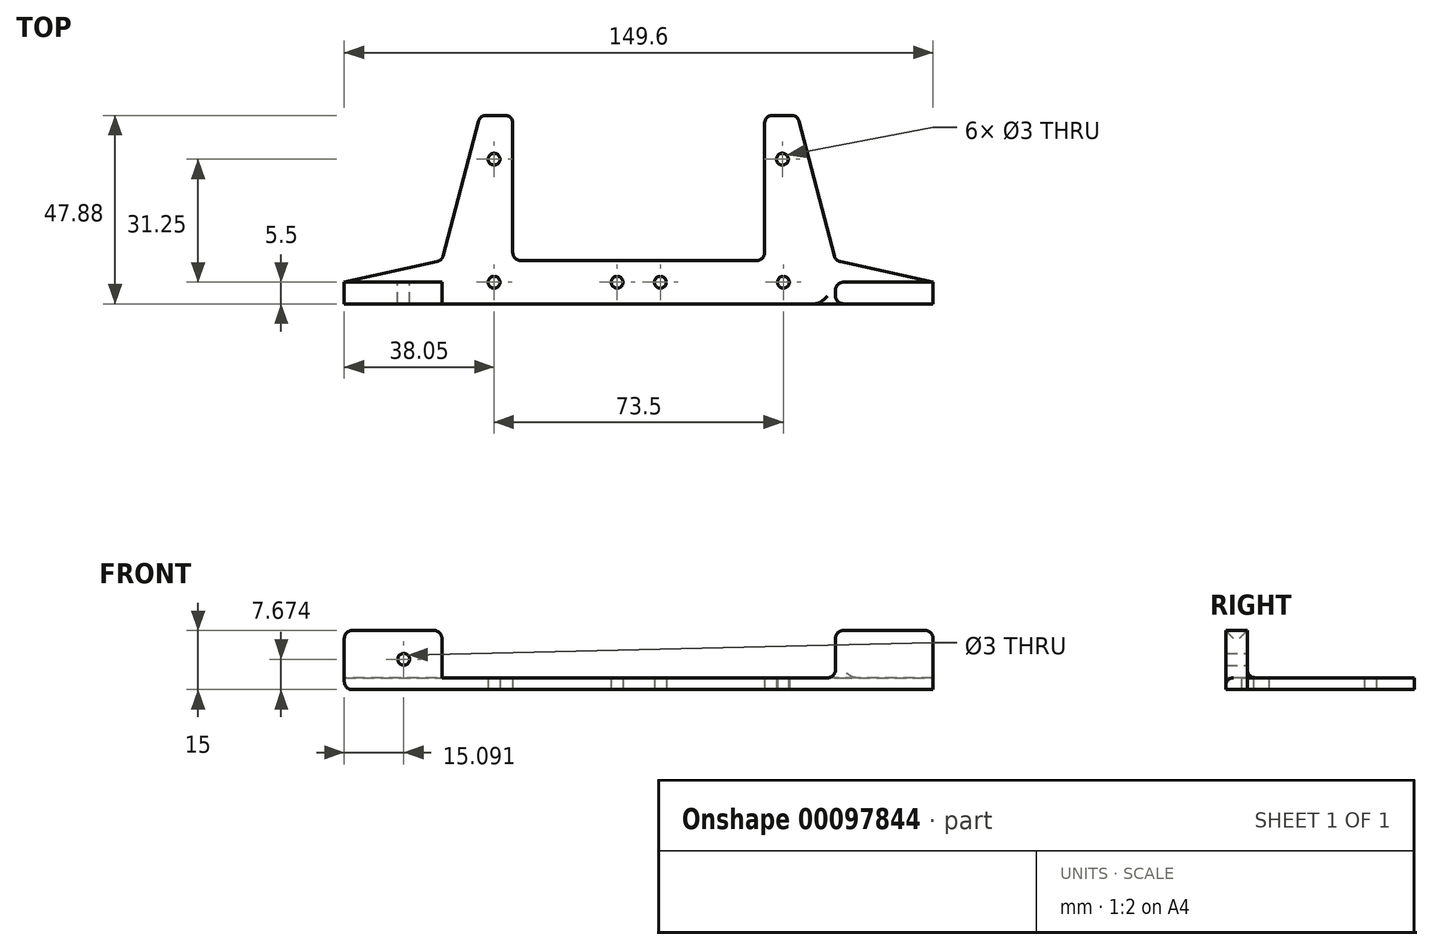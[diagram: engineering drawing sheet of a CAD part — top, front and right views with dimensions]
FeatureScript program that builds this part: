
annotation { "Feature Type Name" : "Feature", "Feature Type Description" : "" }
export const myFeature = defineFeature(function(context is Context, id is Id, definition is map)
    precondition{}
    {
        {
            var Q0;
            Q0=qCreatedBy(makeId("Top.planeOp"),FACE);
            var sketch = newSketch(context, id + "F0", { "sketchPlane" : qUnion([Q0])});
            skCircle(sketch, "E0", {"center": v(-5.5, 0) * mm, "radius": 1.5 * mm});
            skCircle(sketch, "E1", {"center": v(-36.75, 0) * mm, "radius": 1.5 * mm});
            skCircle(sketch, "E2", {"center": v(5.5, 0) * mm, "radius": 1.5 * mm});
            skCircle(sketch, "E3", {"center": v(36.75, 0) * mm, "radius": 1.5 * mm});
            skLineSegment(sketch, "E4", {"start": v(-5.5, 0) * mm, "end": v(5.5, 0) * mm, "construction": true});
            skPoint(sketch, "E5", {"position": v(0, 0) * mm});
            skLineSegment(sketch, "E6.bottom", {"start": v(-50, 5.5) * mm, "end": v(50, 5.5) * mm});
            skLineSegment(sketch, "E6.top", {"start": v(-50, -5.5) * mm, "end": v(50, -5.5) * mm});
            skLineSegment(sketch, "E6.left", {"start": v(-50, 5.5) * mm, "end": v(-50, -5.5) * mm});
            skLineSegment(sketch, "E6.right", {"start": v(50, 5.5) * mm, "end": v(50, -5.5) * mm});
            skPoint(sketch, "E7", {"position": v(50, 0) * mm});
            skPoint(sketch, "E8", {"position": v(0, 5.5) * mm});
            skPoint(sketch, "E9.endSnap0", {"position": v(-50, 0) * mm});
            skPoint(sketch, "E9.end.orphan", {"position": v(-64.27, 0) * mm});
            skPoint(sketch, "E9.start.orphan", {"position": v(-50, 0) * mm});
            skLineSegment(sketch, "E10", {"start": v(-36.75, 0) * mm, "end": v(-36.75, 31.25) * mm, "construction": true});
            skLineSegment(sketch, "E11", {"start": v(-36.75, 31.25) * mm, "end": v(36.5, 31.25) * mm, "construction": true});
            skLineSegment(sketch, "E12", {"start": v(36.5, 31.25) * mm, "end": v(36.75, 0) * mm, "construction": true});
            skCircle(sketch, "E13", {"center": v(-36.75, 31.25) * mm, "radius": 1.5 * mm});
            skCircle(sketch, "E14", {"center": v(36.5, 31.25) * mm, "radius": 1.5 * mm});
            skLineSegment(sketch, "E15", {"start": v(-50, 5.5) * mm, "end": v(-40.35, 42.38) * mm});
            skLineSegment(sketch, "E16", {"start": v(-40.35, 42.38) * mm, "end": v(-32, 42.38) * mm});
            skLineSegment(sketch, "E17", {"start": v(-32, 42.38) * mm, "end": v(-32, 5.5) * mm});
            skLineSegment(sketch, "E18", {"start": v(50, 5.5) * mm, "end": v(40.35, 42.38) * mm});
            skLineSegment(sketch, "E19", {"start": v(40.35, 42.38) * mm, "end": v(32, 42.38) * mm});
            skLineSegment(sketch, "E20", {"start": v(32, 42.38) * mm, "end": v(32, 5.5) * mm});
            skLineSegment(sketch, "E21", {"start": v(50, -5.5) * mm, "end": v(74.8, -5.5) * mm});
            skLineSegment(sketch, "E22", {"start": v(74.8, -5.5) * mm, "end": v(74.8, 0) * mm});
            skLineSegment(sketch, "E23", {"start": v(74.8, 0) * mm, "end": v(50, 0) * mm});
            skLineSegment(sketch, "E24.MirrorCS", {"start": v(-74.8, 0) * mm, "end": v(-50, 0) * mm});
            skLineSegment(sketch, "E25.MirrorCS", {"start": v(-50, -5.5) * mm, "end": v(-74.8, -5.5) * mm});
            skLineSegment(sketch, "E26", {"start": v(-74.8, 0) * mm, "end": v(-74.8, -5.5) * mm});
            skLineSegment(sketch, "E27", {"start": v(-50, 5.5) * mm, "end": v(-74.8, 0) * mm});
            skLineSegment(sketch, "E28", {"start": v(50, 5.5) * mm, "end": v(74.8, 0) * mm});
            skSolve(sketch);
        }
        {
            var Q0;
            {var subQ0=sQuery(id+"F0.wireOp",EDGE,"E15");Q0=makeQuery(id+"F0.imprint","IMPRINT",FACE,{"disambiguationData":[TD([[makeQuery(id+"F0.imprint","IMPRINT",EDGE,{"derivedFrom":subQ0}),-1.0]])]});}
            var Q1;
            Q1=makeQuery(id+"F0.imprint","IMPRINT",FACE,{"disambiguationData":[TD([[makeQuery(id+"F0.imprint","IMPRINT",EDGE,{"derivedFrom":sQuery(id+"F0.wireOp",EDGE,"E0")}),-1.0]])]});
            var Q2;
            {var subQ0=sQuery(id+"F0.wireOp",EDGE,"E18");Q2=makeQuery(id+"F0.imprint","IMPRINT",FACE,{"disambiguationData":[TD([[makeQuery(id+"F0.imprint","IMPRINT",EDGE,{"derivedFrom":subQ0}),1.0]])]});}
            var Q3;
            {var subQ2=sQuery(id+"F0.wireOp",EDGE,"E24.MirrorCS");Q3=makeQuery(id+"F0.imprint","IMPRINT",FACE,{"disambiguationData":[TD([[makeQuery(id+"F0.imprint","IMPRINT",EDGE,{"derivedFrom":subQ2}),1.0]])]});}
            var Q4;
            {var subQ2=sQuery(id+"F0.wireOp",EDGE,"E23");Q4=makeQuery(id+"F0.imprint","IMPRINT",FACE,{"disambiguationData":[TD([[makeQuery(id+"F0.imprint","IMPRINT",EDGE,{"derivedFrom":subQ2}),-1.0]])]});}
            extrude(context, id + "F1", {"entities" : qUnion([Q0, Q1, Q2, Q3, Q4]), "depth" : 3 * mm});
        }
        {
            var Q0;
            {var subQ2=sQuery(id+"F0.wireOp",EDGE,"E24.MirrorCS");Q0=makeQuery(id+"F0.imprint","IMPRINT",FACE,{"disambiguationData":[TD([[makeQuery(id+"F0.imprint","IMPRINT",EDGE,{"derivedFrom":subQ2}),-1.0]])]});}
            var Q1;
            {var subQ0=sQuery(id+"F0.wireOp",EDGE,"E21");Q1=makeQuery(id+"F0.imprint","IMPRINT",FACE,{"disambiguationData":[TD([[makeQuery(id+"F0.imprint","IMPRINT",EDGE,{"derivedFrom":subQ0}),1.0]])]});}
            extrude(context, id + "F2", {"entities" : qUnion([Q0, Q1]), "operationType" : NewBodyOperationType.ADD, "depth" : 15 * mm});
        }
        {
            var Q0;
            Q0=qCreatedBy(makeId("Front.planeOp"),FACE);
            var sketch = newSketch(context, id + "F3", { "sketchPlane" : qUnion([Q0])});
            skCircle(sketch, "E29", {"center": v(-59.7, 7.67) * mm, "radius": 1.5 * mm});
            skLineSegment(sketch, "E30", {"start": v(-74.7, 0) * mm, "end": v(-74.7, 7.5) * mm});
            skLineSegment(sketch, "E31", {"start": v(-74.7, 7.5) * mm, "end": v(-59.7, 7.67) * mm});
            skLineSegment(sketch, "E32.MirrorCS", {"start": v(74.7, 0) * mm, "end": v(74.7, 7.5) * mm});
            skLineSegment(sketch, "E33.MirrorCS", {"start": v(74.7, 7.5) * mm, "end": v(59.7, 7.67) * mm});
            skCircle(sketch, "E34.MirrorC", {"center": v(59.7, 7.67) * mm, "radius": 1.5 * mm});
            skSolve(sketch);
        }
        {
            var Q0;
            Q0=makeQuery(id+"F3.imprint","IMPRINT",FACE,{"disambiguationData":[TD([[makeQuery(id+"F3.imprint","IMPRINT",EDGE,{"derivedFrom":sQuery(id+"F3.wireOp",EDGE,"E34.MirrorC")}),-1.0]])]});
            var Q1;
            Q1=makeQuery(id+"F3.imprint","IMPRINT",FACE,{"disambiguationData":[TD([[makeQuery(id+"F3.imprint","IMPRINT",EDGE,{"derivedFrom":sQuery(id+"F3.wireOp",EDGE,"E29")}),1.0]])]});
            extrude(context, id + "F4", {"entities" : qUnion([Q0, Q1]), "operationType" : NewBodyOperationType.REMOVE, "depth" : 25 * mm});
        }
        {
            var Q0;
            Q0=makeQuery(id+"F1.opExtrude","SWEPT_EDGE",EDGE,{"disambiguationData":[OSD([sQuery(id+"F0.wireOp",EDGE,"E6.top"),sQuery(id+"F0.wireOp",EDGE,"E6.right")])]});
            var Q1;
            Q1=makeQuery(id+"F1.opExtrude","SWEPT_EDGE",EDGE,{"disambiguationData":[OSD([sQuery(id+"F0.wireOp",EDGE,"E6.bottom"),sQuery(id+"F0.wireOp",EDGE,"E6.right"),sQuery(id+"F0.wireOp",EDGE,"E18")])]});
            var Q2;
            Q2=makeQuery(id+"F1.opExtrude","SWEPT_EDGE",EDGE,{"disambiguationData":[OSD([sQuery(id+"F0.wireOp",EDGE,"E18"),sQuery(id+"F0.wireOp",EDGE,"E19")])]});
            var Q3;
            Q3=makeQuery(id+"F1.opExtrude","SWEPT_EDGE",EDGE,{"disambiguationData":[OSD([sQuery(id+"F0.wireOp",EDGE,"E19"),sQuery(id+"F0.wireOp",EDGE,"E20")])]});
            var Q4;
            Q4=makeQuery(id+"F1.opExtrude","SWEPT_EDGE",EDGE,{"disambiguationData":[OSD([sQuery(id+"F0.wireOp",EDGE,"E6.bottom"),sQuery(id+"F0.wireOp",EDGE,"E20")])]});
            var Q5;
            Q5=makeQuery(id+"F1.opExtrude","SWEPT_EDGE",EDGE,{"disambiguationData":[OSD([sQuery(id+"F0.wireOp",EDGE,"E6.bottom"),sQuery(id+"F0.wireOp",EDGE,"E17")])]});
            var Q6;
            Q6=makeQuery(id+"F1.opExtrude","SWEPT_EDGE",EDGE,{"disambiguationData":[OSD([sQuery(id+"F0.wireOp",EDGE,"E16"),sQuery(id+"F0.wireOp",EDGE,"E17")])]});
            var Q7;
            Q7=makeQuery(id+"F1.opExtrude","SWEPT_EDGE",EDGE,{"disambiguationData":[OSD([sQuery(id+"F0.wireOp",EDGE,"E15"),sQuery(id+"F0.wireOp",EDGE,"E16")])]});
            var Q8;
            Q8=makeQuery(id+"F1.opExtrude","SWEPT_EDGE",EDGE,{"disambiguationData":[OSD([sQuery(id+"F0.wireOp",EDGE,"E6.bottom"),sQuery(id+"F0.wireOp",EDGE,"E6.left"),sQuery(id+"F0.wireOp",EDGE,"E15")])]});
            var Q9;
            Q9=makeQuery(id+"F1.opExtrude","SWEPT_EDGE",EDGE,{"disambiguationData":[OSD([sQuery(id+"F0.wireOp",EDGE,"E6.top"),sQuery(id+"F0.wireOp",EDGE,"E6.left")])]});
            var Q10;
            Q10=makeQuery(id+"F2.opExtrude","CAP_EDGE",EDGE,{"disambiguationData":[OSD([sQuery(id+"F0.wireOp",EDGE,"E26")])],"isStart":false});
            var Q11;
            Q11=makeQuery(id+"F2.opExtrude","CAP_EDGE",EDGE,{"disambiguationData":[OSD([sQuery(id+"F0.wireOp",EDGE,"E6.left")])],"isStart":false});
            var Q12;
            Q12=makeQuery(id+"F1.opExtrude","CAP_EDGE",EDGE,{"disambiguationData":[OSD([sQuery(id+"F0.wireOp",EDGE,"E6.left")])],"isStart":false});
            var Q13;
            Q13=makeQuery(id+"F2.opExtrude","CAP_EDGE",EDGE,{"disambiguationData":[OSD([sQuery(id+"F0.wireOp",EDGE,"E26")])],"isStart":true});
            var Q14;
            Q14=makeQuery(id+"F2.opExtrude","SWEPT_FACE",FACE,{"disambiguationData":[OSD([sQuery(id+"F0.wireOp",EDGE,"E6.right")])]});
            var Q15;
            Q15=makeQuery(id+"F2.opExtrude","CAP_EDGE",EDGE,{"disambiguationData":[OSD([sQuery(id+"F0.wireOp",EDGE,"E22")])],"isStart":false});
            var Q16;
            Q16=makeQuery(id+"F2.opExtrude","SWEPT_EDGE",EDGE,{"disambiguationData":[OSD([sQuery(id+"F0.wireOp",EDGE,"E6.right"),sQuery(id+"F0.wireOp",EDGE,"E23")])]});
            fillet(context, id + "F5", {"entities" : qUnion([Q0, Q1, Q2, Q3, Q4, Q5, Q6, Q7, Q8, Q9, Q10, Q11, Q12, Q13, Q14, Q15, Q16]), "radius" : 2 * mm, "tangentPropagation" : true, "allowEdgeOverflow" : false});
        }
    });
